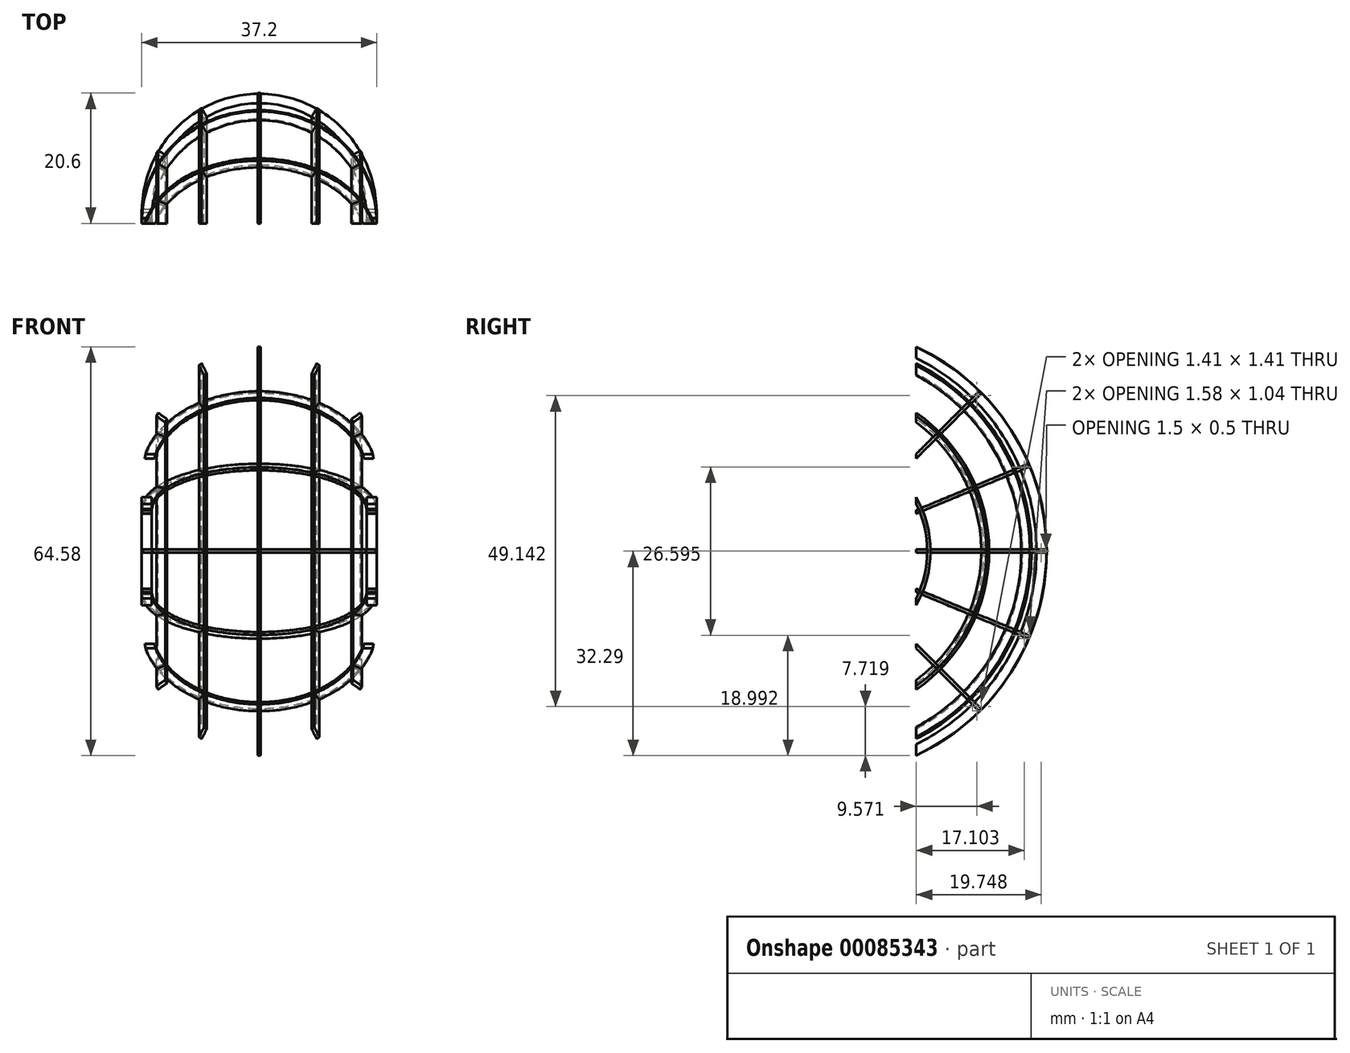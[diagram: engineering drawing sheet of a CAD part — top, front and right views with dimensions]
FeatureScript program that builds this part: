
annotation { "Feature Type Name" : "Feature", "Feature Type Description" : "" }
export const myFeature = defineFeature(function(context is Context, id is Id, definition is map)
    precondition{}
    {
        {
            var Q0;
            Q0=qCreatedBy(makeId("Right.planeOp"),FACE);
            var sketch = newSketch(context, id + "F0", { "sketchPlane" : qUnion([Q0])});
            skCircle(sketch, "E0", {"center": v(0, 0) * mm, "radius": 34 * mm, "construction": true});
            skLineSegment(sketch, "E1", {"start": v(48.44, 17) * mm, "end": v(-86.61, 17) * mm, "construction": true});
            skSolve(sketch);
        }
        {
            var Q0;
            Q0=qCreatedBy(makeId("Front.planeOp"),FACE);
            var sketch = newSketch(context, id + "F1", { "sketchPlane" : qUnion([Q0])});
            skArc(sketch, "E2", {"start": v(-8.28, 31.85) * mm, "mid": v(-8.5, 31.72) * mm, "end": v(-8.72, 31.6) * mm});
            skArc(sketch, "E3", {"start": v(-9.08, 33.23) * mm, "mid": v(-9.3, 33.1) * mm, "end": v(-9.52, 32.98) * mm});
            skLineSegment(sketch, "E4", {"start": v(0, 17) * mm, "end": v(-10.5, 35.18) * mm, "construction": true});
            skLineSegment(sketch, "E5", {"start": v(0, 17) * mm, "end": v(-17.75, 27.25) * mm, "construction": true});
            skLineSegment(sketch, "E6", {"start": v(0, 17) * mm, "end": v(-21.32, 17) * mm, "construction": true});
            skLineSegment(sketch, "E7", {"start": v(0, 17) * mm, "end": v(-16.1, 7.7) * mm, "construction": true});
            skLineSegment(sketch, "E8", {"start": v(0, 17) * mm, "end": v(-10.04, -0.4) * mm, "construction": true});
            skLineSegment(sketch, "E9", {"start": v(0, 17) * mm, "end": v(10.96, 35.98) * mm, "construction": true});
            skLineSegment(sketch, "E10", {"start": v(0, 17) * mm, "end": v(21.73, 4.45) * mm, "construction": true});
            skLineSegment(sketch, "E11", {"start": v(0, 17) * mm, "end": v(11.8, -3.45) * mm, "construction": true});
            skLineSegment(sketch, "E12", {"start": v(0, 17) * mm, "end": v(25.6, 17) * mm, "construction": true});
            skLineSegment(sketch, "E13", {"start": v(0, 17) * mm, "end": v(21.84, 29.6) * mm, "construction": true});
            skLineSegment(sketch, "E14", {"start": v(0, 37.24) * mm, "end": v(0, -4.97) * mm, "construction": true});
            skLineSegment(sketch, "E15", {"start": v(-0.25, 35.6) * mm, "end": v(-0.25, 34) * mm});
            skLineSegment(sketch, "E16", {"start": v(0.25, 35.6) * mm, "end": v(0.25, 34) * mm});
            skLineSegment(sketch, "E17", {"start": v(-9.08, 33.23) * mm, "end": v(-8.28, 31.85) * mm});
            skLineSegment(sketch, "E18", {"start": v(-9.52, 32.98) * mm, "end": v(-8.72, 31.6) * mm});
            skLineSegment(sketch, "E19", {"start": v(-15.98, 26.52) * mm, "end": v(-14.6, 25.72) * mm});
            skLineSegment(sketch, "E20", {"start": v(-16.23, 26.08) * mm, "end": v(-14.85, 25.28) * mm});
            skLineSegment(sketch, "E21", {"start": v(-18.6, 17.25) * mm, "end": v(-17, 17.25) * mm});
            skLineSegment(sketch, "E22", {"start": v(-18.6, 16.75) * mm, "end": v(-17, 16.75) * mm});
            skLineSegment(sketch, "E23", {"start": v(-14.85, 8.72) * mm, "end": v(-16.23, 7.92) * mm});
            skLineSegment(sketch, "E24", {"start": v(-14.6, 8.28) * mm, "end": v(-15.98, 7.48) * mm});
            skLineSegment(sketch, "E25", {"start": v(-8.72, 2.4) * mm, "end": v(-9.52, 1.02) * mm});
            skLineSegment(sketch, "E26", {"start": v(-8.28, 2.15) * mm, "end": v(-9.08, 0.77) * mm});
            skLineSegment(sketch, "E27", {"start": v(-0.25, 0) * mm, "end": v(-0.25, -1.6) * mm});
            skLineSegment(sketch, "E28", {"start": v(0.25, 0) * mm, "end": v(0.25, -1.6) * mm});
            skLineSegment(sketch, "E29", {"start": v(8.28, 2.15) * mm, "end": v(9.08, 0.77) * mm});
            skLineSegment(sketch, "E30", {"start": v(8.72, 2.4) * mm, "end": v(9.52, 1.02) * mm});
            skLineSegment(sketch, "E31", {"start": v(14.6, 8.28) * mm, "end": v(15.98, 7.48) * mm});
            skLineSegment(sketch, "E32", {"start": v(14.85, 8.72) * mm, "end": v(16.23, 7.92) * mm});
            skLineSegment(sketch, "E33", {"start": v(17, 16.75) * mm, "end": v(18.6, 16.75) * mm});
            skLineSegment(sketch, "E34", {"start": v(17, 17.25) * mm, "end": v(18.6, 17.25) * mm});
            skLineSegment(sketch, "E35", {"start": v(16.23, 26.08) * mm, "end": v(14.85, 25.28) * mm});
            skLineSegment(sketch, "E36", {"start": v(15.98, 26.52) * mm, "end": v(14.6, 25.72) * mm});
            skLineSegment(sketch, "E37", {"start": v(9.52, 32.98) * mm, "end": v(8.72, 31.6) * mm});
            skLineSegment(sketch, "E38", {"start": v(9.08, 33.23) * mm, "end": v(8.28, 31.85) * mm});
            skArc(sketch, "E39.trimOffspring", {"start": v(-15.98, 26.52) * mm, "mid": v(-16.1, 26.3) * mm, "end": v(-16.23, 26.08) * mm});
            skArc(sketch, "E40.trimOffspring", {"start": v(-14.6, 25.72) * mm, "mid": v(-14.72, 25.5) * mm, "end": v(-14.85, 25.28) * mm});
            skArc(sketch, "E41.trimOffspring", {"start": v(-18.6, 17.25) * mm, "mid": v(-18.6, 17) * mm, "end": v(-18.6, 16.75) * mm});
            skArc(sketch, "E42.trimOffspring", {"start": v(-17, 17.25) * mm, "mid": v(-17, 17) * mm, "end": v(-17, 16.75) * mm});
            skArc(sketch, "E43.trimOffspring", {"start": v(-16.23, 7.92) * mm, "mid": v(-16.1, 7.7) * mm, "end": v(-15.98, 7.48) * mm});
            skArc(sketch, "E44.trimOffspring", {"start": v(-14.85, 8.72) * mm, "mid": v(-14.72, 8.5) * mm, "end": v(-14.6, 8.28) * mm});
            skArc(sketch, "E45.trimOffspring", {"start": v(-8.72, 2.4) * mm, "mid": v(-8.5, 2.28) * mm, "end": v(-8.28, 2.15) * mm});
            skArc(sketch, "E46.trimOffspring", {"start": v(-9.52, 1.02) * mm, "mid": v(-9.3, 0.9) * mm, "end": v(-9.08, 0.77) * mm});
            skArc(sketch, "E47.trimOffspring", {"start": v(-0.25, 0) * mm, "mid": v(0, 0) * mm, "end": v(0.25, 0) * mm});
            skArc(sketch, "E48.trimOffspring", {"start": v(-0.25, -1.6) * mm, "mid": v(0, -1.6) * mm, "end": v(0.25, -1.6) * mm});
            skArc(sketch, "E49.trimOffspring", {"start": v(8.28, 2.15) * mm, "mid": v(8.5, 2.28) * mm, "end": v(8.72, 2.4) * mm});
            skArc(sketch, "E50.trimOffspring", {"start": v(9.08, 0.77) * mm, "mid": v(9.3, 0.9) * mm, "end": v(9.52, 1.02) * mm});
            skArc(sketch, "E51.trimOffspring", {"start": v(15.98, 7.48) * mm, "mid": v(16.1, 7.7) * mm, "end": v(16.23, 7.92) * mm});
            skArc(sketch, "E52.trimOffspring", {"start": v(14.6, 8.28) * mm, "mid": v(14.66, 8.4) * mm, "end": v(14.72, 8.5) * mm});
            skArc(sketch, "E53.trimOffspring", {"start": v(18.6, 16.75) * mm, "mid": v(18.6, 17) * mm, "end": v(18.6, 17.25) * mm});
            skArc(sketch, "E54.trimOffspring", {"start": v(17, 16.75) * mm, "mid": v(17, 17) * mm, "end": v(17, 17.25) * mm});
            skArc(sketch, "E55.trimOffspring", {"start": v(16.23, 26.08) * mm, "mid": v(16.1, 26.3) * mm, "end": v(15.98, 26.52) * mm});
            skArc(sketch, "E56.trimOffspring", {"start": v(14.85, 25.28) * mm, "mid": v(14.72, 25.5) * mm, "end": v(14.6, 25.72) * mm});
            skArc(sketch, "E57.trimOffspring", {"start": v(9.52, 32.98) * mm, "mid": v(9.3, 33.1) * mm, "end": v(9.08, 33.23) * mm});
            skArc(sketch, "E58.trimOffspring", {"start": v(8.72, 31.6) * mm, "mid": v(8.5, 31.72) * mm, "end": v(8.28, 31.85) * mm});
            skArc(sketch, "E59.trimOffspring", {"start": v(0.25, 35.6) * mm, "mid": v(0, 35.6) * mm, "end": v(-0.25, 35.6) * mm});
            skArc(sketch, "E60.trimOffspring", {"start": v(0.25, 34) * mm, "mid": v(0, 34) * mm, "end": v(-0.25, 34) * mm});
            skLineSegment(sketch, "E61", {"start": v(-41.35, 0) * mm, "end": v(40.72, 0) * mm, "construction": true});
            skArc(sketch, "E62", {"start": v(14.72, 8.5) * mm, "mid": v(14.78, 8.6) * mm, "end": v(14.85, 8.72) * mm});
            skSolve(sketch);
        }
        {
            var Q0;
            Q0=makeQuery(id+"F1.imprint","IMPRINT",FACE,{"disambiguationData":[TD([[makeQuery(id+"F1.imprint","IMPRINT",EDGE,{"derivedFrom":sQuery(id+"F1.wireOp",EDGE,"E2")}),-1.0]])]});
            var Q1;
            Q1=makeQuery(id+"F1.imprint","IMPRINT",FACE,{"disambiguationData":[TD([[makeQuery(id+"F1.imprint","IMPRINT",EDGE,{"derivedFrom":sQuery(id+"F1.wireOp",EDGE,"E15")}),1.0]])]});
            var Q2;
            Q2=makeQuery(id+"F1.imprint","IMPRINT",FACE,{"disambiguationData":[TD([[makeQuery(id+"F1.imprint","IMPRINT",EDGE,{"derivedFrom":sQuery(id+"F1.wireOp",EDGE,"E25")}),1.0]])]});
            var Q3;
            Q3=makeQuery(id+"F1.imprint","IMPRINT",FACE,{"disambiguationData":[TD([[makeQuery(id+"F1.imprint","IMPRINT",EDGE,{"derivedFrom":sQuery(id+"F1.wireOp",EDGE,"E35")}),-1.0]])]});
            var Q4;
            Q4=makeQuery(id+"F1.imprint","IMPRINT",FACE,{"disambiguationData":[TD([[makeQuery(id+"F1.imprint","IMPRINT",EDGE,{"derivedFrom":sQuery(id+"F1.wireOp",EDGE,"E37")}),-1.0]])]});
            var Q5;
            Q5=makeQuery(id+"F1.imprint","IMPRINT",FACE,{"disambiguationData":[TD([[makeQuery(id+"F1.imprint","IMPRINT",EDGE,{"derivedFrom":sQuery(id+"F1.wireOp",EDGE,"E33")}),1.0]])]});
            var Q6;
            Q6=makeQuery(id+"F1.imprint","IMPRINT",FACE,{"disambiguationData":[TD([[makeQuery(id+"F1.imprint","IMPRINT",EDGE,{"derivedFrom":sQuery(id+"F1.wireOp",EDGE,"E21")}),-1.0]])]});
            var Q7;
            Q7=makeQuery(id+"F1.imprint","IMPRINT",FACE,{"disambiguationData":[TD([[makeQuery(id+"F1.imprint","IMPRINT",EDGE,{"derivedFrom":sQuery(id+"F1.wireOp",EDGE,"E19")}),-1.0]])]});
            var Q8;
            Q8=makeQuery(id+"F1.imprint","IMPRINT",FACE,{"disambiguationData":[TD([[makeQuery(id+"F1.imprint","IMPRINT",EDGE,{"derivedFrom":sQuery(id+"F1.wireOp",EDGE,"E23")}),1.0]])]});
            var Q9;
            Q9=makeQuery(id+"F1.imprint","IMPRINT",FACE,{"disambiguationData":[TD([[makeQuery(id+"F1.imprint","IMPRINT",EDGE,{"derivedFrom":sQuery(id+"F1.wireOp",EDGE,"E31")}),1.0]])]});
            var Q10;
            Q10=makeQuery(id+"F1.imprint","IMPRINT",FACE,{"disambiguationData":[TD([[makeQuery(id+"F1.imprint","IMPRINT",EDGE,{"derivedFrom":sQuery(id+"F1.wireOp",EDGE,"E29")}),1.0]])]});
            var Q11;
            Q11=sQuery(id+"F1.wireOp",EDGE,"E61");
            revolve(context, id + "F2", {"entities" : qUnion([Q0, Q1, Q2, Q3, Q4, Q5, Q6, Q7, Q8, Q9, Q10]), "axis" : qUnion([Q11]), "revolveType" : RevolveType.ONE_DIRECTION, "oppositeDirection" : true, "angle" : 180 * degree});
        }
        {
            var Q0;
            Q0=qCreatedBy(makeId("Front.planeOp"),FACE);
            var sketch = newSketch(context, id + "F3", { "sketchPlane" : qUnion([Q0])});
            skCircle(sketch, "E63", {"center": v(0, 17) * mm, "radius": 17 * mm});
            skCircle(sketch, "E64", {"center": v(0, 17) * mm, "radius": 18.5 * mm});
            skSolve(sketch);
        }
        {
            var Q0;
            Q0 = qSketchRegion(id + "F3", true);
            extrude(context, id + "F4", {"entities" : qUnion([Q0]), "depth" : .5 * mm, "symmetric" : true});
        }
        {
            var Q0;
            Q0=makeQuery(id+"F4.opExtrude","SWEPT_BODY",BODY,{"disambiguationData":[OSD([sQuery(id+"F3.wireOp",EDGE,"E63"),sQuery(id+"F3.wireOp",EDGE,"E64")])]});
            var Q1;
            Q1=sQuery(id+"F1.wireOp",EDGE,"E61");
            circularPattern(context, id + "F5", {"operationType" : NewBodyOperationType.ADD, "entities" : qUnion([Q0]), "axis" : qUnion([Q1]), "angle" : 22.5 * degree, "instanceCount" : 9, "oppositeDirection" : true, "computeTransformsWithoutBuiltin" : true});
        }
        {
            var Q0;
            Q0=qCreatedBy(makeId("Right.planeOp"),FACE);
            var sketch = newSketch(context, id + "F6", { "sketchPlane" : qUnion([Q0])});
            skLineSegment(sketch, "E65.bottom", {"start": v(15, 40) * mm, "end": v(-5, 40) * mm});
            skLineSegment(sketch, "E65.top", {"start": v(15, -40) * mm, "end": v(-5, -40) * mm});
            skLineSegment(sketch, "E65.left", {"start": v(15, 40) * mm, "end": v(15, -40) * mm});
            skLineSegment(sketch, "E65.right", {"start": v(-5, 40) * mm, "end": v(-5, -40) * mm});
            skLineSegment(sketch, "E66", {"start": v(0, 0) * mm, "end": v(43.71, 0) * mm, "construction": true});
            skSolve(sketch);
        }
        {
            var Q0;
            Q0 = qSketchRegion(id + "F6", true);
            extrude(context, id + "F7", {"entities" : qUnion([Q0]), "operationType" : NewBodyOperationType.REMOVE, "oppositeDirection" : true, "depth" : 50 * mm, "symmetric" : true});
        }
    });
